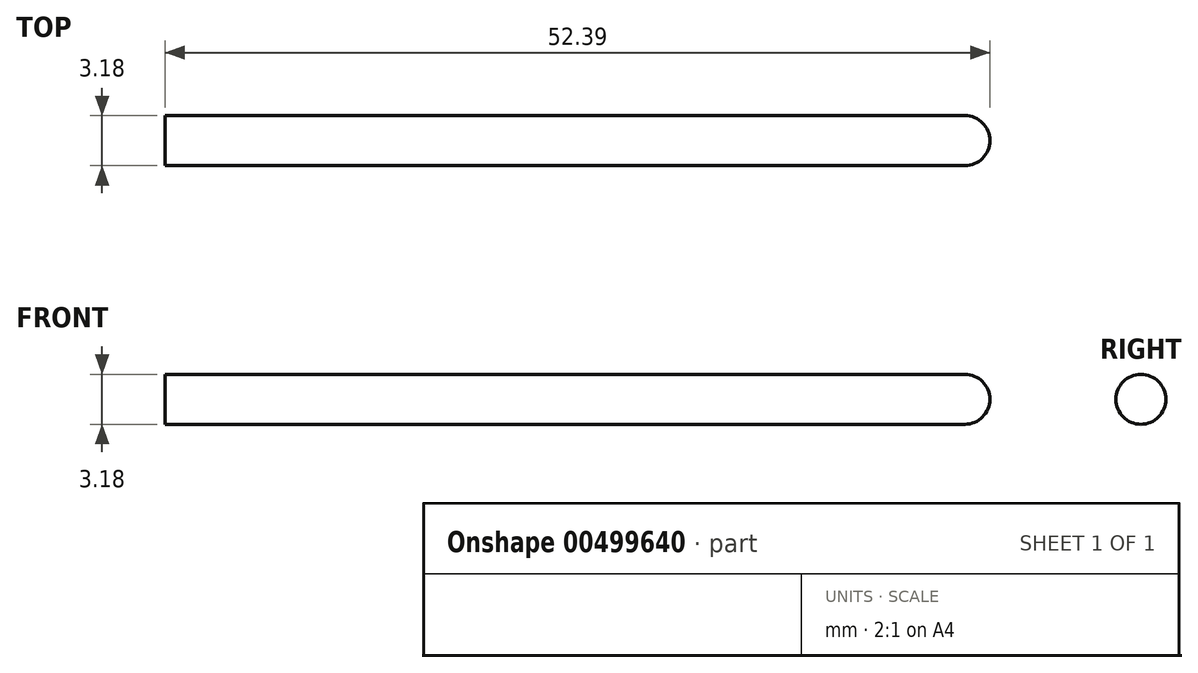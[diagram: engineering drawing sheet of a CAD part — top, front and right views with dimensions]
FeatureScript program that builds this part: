
annotation { "Feature Type Name" : "Feature", "Feature Type Description" : "" }
export const myFeature = defineFeature(function(context is Context, id is Id, definition is map)
    precondition{}
    {
        {
            var Q0;
            Q0=qCreatedBy(makeId("Right.planeOp"),FACE);
            var sketch = newSketch(context, id + "F0", { "sketchPlane" : qUnion([Q0])});
            skCircle(sketch, "E0", {"center": v(0, 0) * mm, "radius": 1.59 * mm});
            skSolve(sketch);
        }
        {
            var Q0;
            Q0 = qSketchRegion(id + "F0", true);
            extrude(context, id + "F1", {"entities" : qUnion([Q0]), "depth" : 50.8 * mm});
        }
        {
            var Q0;
            Q0=makeQuery(id+"F1.opExtrude","CAP_FACE",FACE,{"disambiguationData":[OSD([sQuery(id+"F0.wireOp",EDGE,"E0")])],"isStart":false});
            var sketch = newSketch(context, id + "F2", { "sketchPlane" : qUnion([Q0])});
            skArc(sketch, "E1", {"start": v(1.59, 0) * mm, "mid": v(0, 1.59) * mm, "end": v(-1.59, 0) * mm});
            skLineSegment(sketch, "E2", {"start": v(-1.59, 0) * mm, "end": v(1.59, 0) * mm});
            skSolve(sketch);
        }
        {
            var Q0;
            Q0=makeQuery(id+"F2.imprint","IMPRINT",FACE,{"disambiguationData":[TD([[makeQuery(id+"F2.imprint","IMPRINT",EDGE,{"derivedFrom":sQuery(id+"F2.wireOp",EDGE,"E1")}),1.0]])]});
            var Q1;
            Q1=sQuery(id+"F2.wireOp",EDGE,"E2");
            revolve(context, id + "F3", {"operationType" : NewBodyOperationType.ADD, "entities" : qUnion([Q0]), "axis" : qUnion([Q1]), "revolveType" : RevolveType.FULL});
        }
    });
